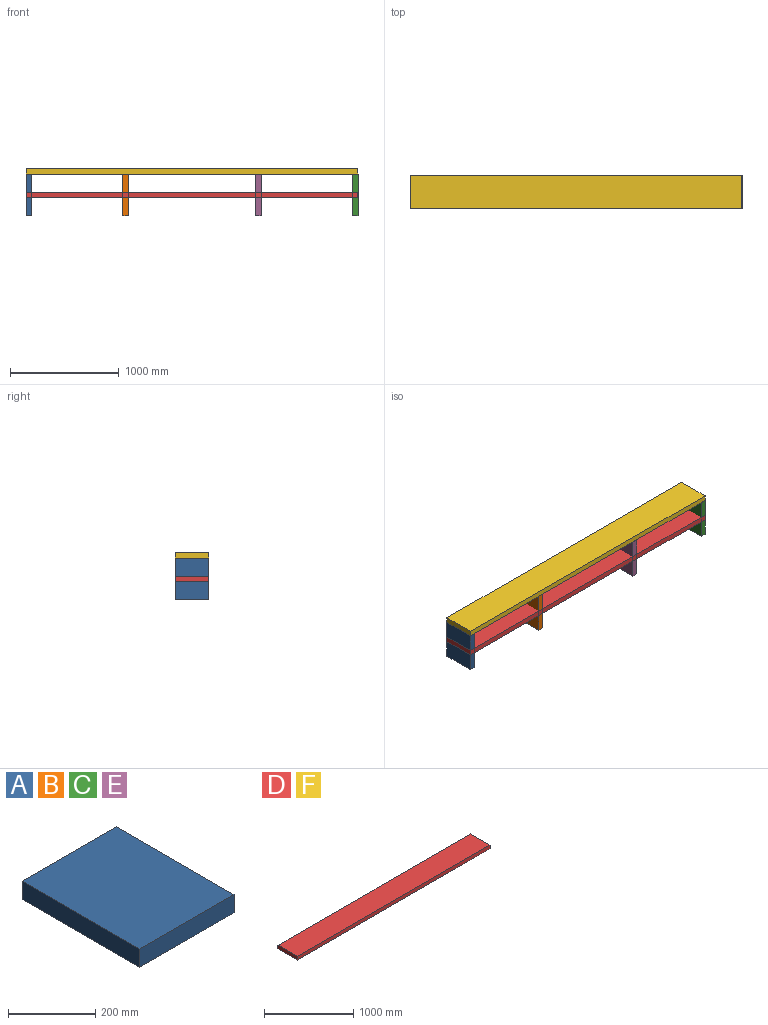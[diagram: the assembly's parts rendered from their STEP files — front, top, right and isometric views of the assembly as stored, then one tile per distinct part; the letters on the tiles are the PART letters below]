
ASSEMBLY  parts=6 mates=5
PART A: 6 faces, bbox 304.8x381x50.8 mm
  f0: plane 304.8x50.8mm, normal (0,1,0), area 15483.8mm2, adj f1,f3,f4,f5
  f1: plane 381x50.8mm, normal (-1,0,0), area 19354.8mm2, adj f0,f2,f4,f5
  f2: plane 304.8x50.8mm, normal (0,-1,0), area 15483.8mm2, adj f1,f3,f4,f5
  f3: plane 381x50.8mm, normal (1,0,0), area 19354.8mm2, adj f0,f2,f4,f5
  f4: plane 381x304.8mm, normal (0,0,1), area 116128.8mm2, adj f0,f1,f2,f3
  f5: plane 381x304.8mm, normal (0,0,-1), area 116128.8mm2, adj f0,f1,f2,f3
PART B: same geometry as A
PART C: same geometry as A
PART D: 6 faces, bbox 3048x304.8x50.8 mm
  f0: plane 3048x50.8mm, normal (0,1,0), area 154838.4mm2, adj f1,f3,f4,f5
  f1: plane 304.8x50.8mm, normal (-1,0,0), area 15483.8mm2, adj f0,f2,f4,f5
  f2: plane 3048x50.8mm, normal (0,-1,0), area 154838.4mm2, adj f1,f3,f4,f5
  f3: plane 304.8x50.8mm, normal (1,0,0), area 15483.8mm2, adj f0,f2,f4,f5
  f4: plane 3048x304.8mm, normal (0,0,1), area 929030.4mm2, adj f0,f1,f2,f3
  f5: plane 3048x304.8mm, normal (0,0,-1), area 929030.4mm2, adj f0,f1,f2,f3
PART E: same geometry as A
PART F: same geometry as D
PLACE A rot(axis=(-0.58,0.58,-0.58),120deg) t=(-1935.66,-178.86,-104.22)mm
PLACE B rot(axis=(-0.58,0.58,-0.58),120deg) t=(-1046.66,-178.86,-104.22)mm
PLACE C rot(axis=(-0.58,0.58,-0.58),120deg) t=(1061.54,-178.86,-104.22)mm
PLACE D t=(-406.15,-118.41,-133.07)mm
PLACE E rot(axis=(-0.58,0.58,-0.58),120deg) t=(172.54,-178.86,-104.22)mm
PLACE F t=(-406.15,-118.41,82.83)mm
MATE fastened B.f2 <-> F.f5  axis (0,0,1) through (-1021.26,-154.52,82.83)mm
MATE fastened C.f2 <-> F.f5  axis (0,0,1) through (1086.94,-154.52,82.83)mm
MATE fastened D.f1 <-> A.f5  axis (-1,0,0) through (-1935.66,-154.52,-107.67)mm
MATE fastened E.f2 <-> F.f5  axis (0,0,1) through (197.94,-154.52,82.83)mm
MATE fastened A.f2 <-> F.f5  axis (0,0,1) through (-1910.26,-154.52,82.83)mm
